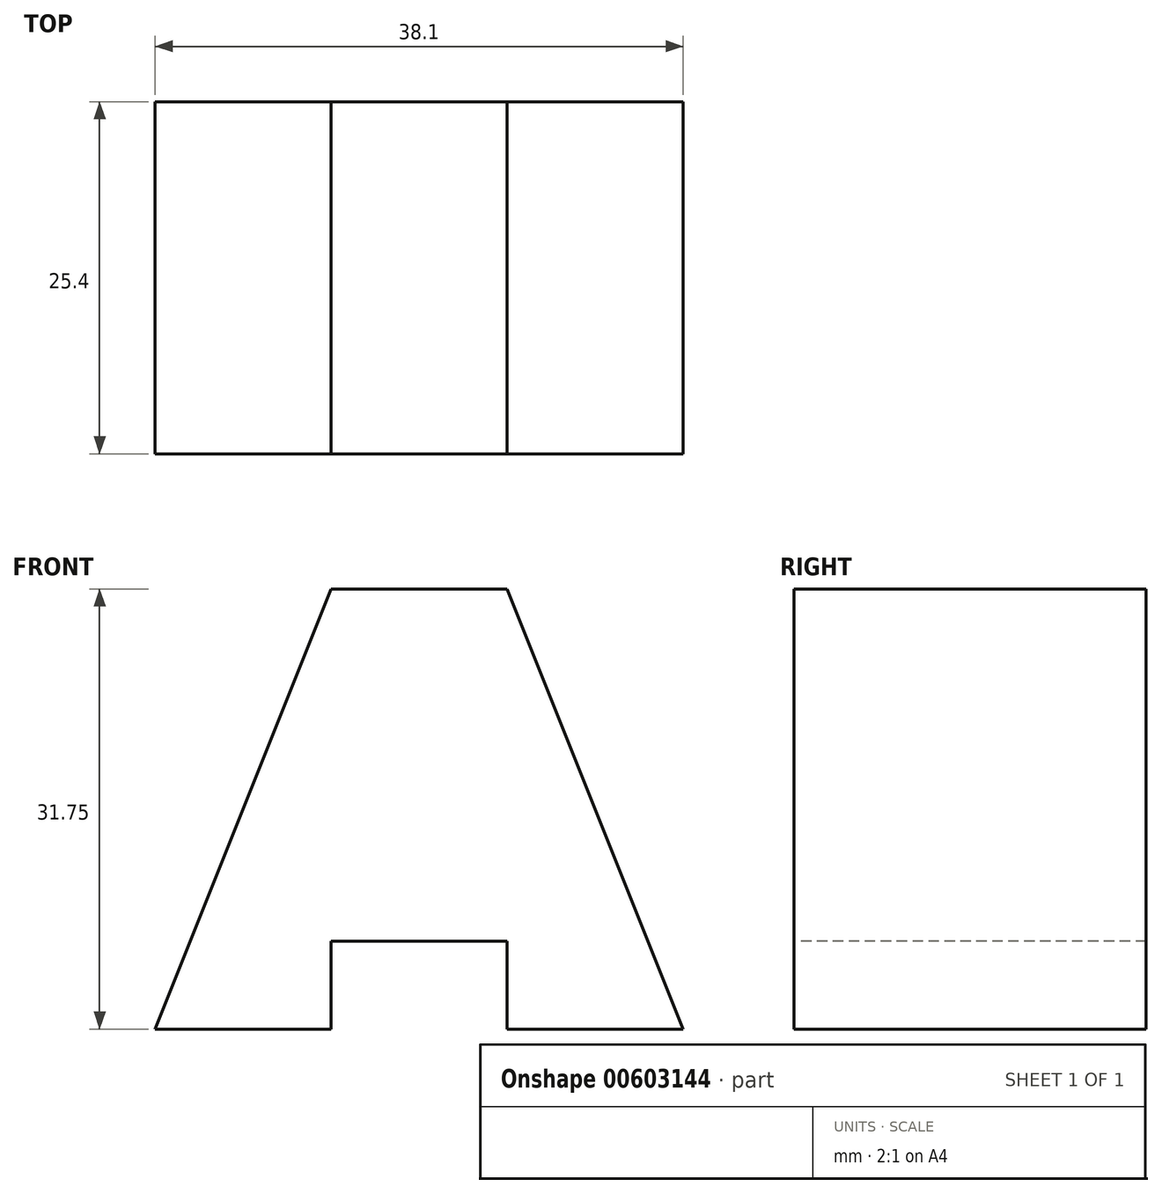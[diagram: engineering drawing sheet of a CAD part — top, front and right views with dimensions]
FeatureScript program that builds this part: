
annotation { "Feature Type Name" : "Feature", "Feature Type Description" : "" }
export const myFeature = defineFeature(function(context is Context, id is Id, definition is map)
    precondition{}
    {
        {
            var Q0;
            Q0=qCreatedBy(makeId("Front.planeOp"),FACE);
            var sketch = newSketch(context, id + "F0", { "sketchPlane" : qUnion([Q0])});
            skLineSegment(sketch, "E0", {"start": v(0, 0) * mm, "end": v(-19.05, 0) * mm});
            skLineSegment(sketch, "E1", {"start": v(-19.05, 0) * mm, "end": v(19.05, 0) * mm});
            skLineSegment(sketch, "E2", {"start": v(19.05, 0) * mm, "end": v(19.05, -31.75) * mm});
            skLineSegment(sketch, "E3", {"start": v(19.05, -31.75) * mm, "end": v(-19.05, -31.75) * mm});
            skLineSegment(sketch, "E4", {"start": v(-19.05, -31.75) * mm, "end": v(-19.05, 0) * mm});
            skSolve(sketch);
        }
        {
            var Q0;
            Q0 = qSketchRegion(id + "F0", true);
            extrude(context, id + "F1", {"entities" : qUnion([Q0]), "depth" : 25.4 * mm, "offsetDistance" : 25.4 * mm});
        }
        {
            var Q0;
            Q0=makeQuery(id+"F1.opExtrude","CAP_FACE",FACE,{"disambiguationData":[OSD([sQuery(id+"F0.wireOp",EDGE,"E1"),sQuery(id+"F0.wireOp",EDGE,"E2"),sQuery(id+"F0.wireOp",EDGE,"E3"),sQuery(id+"F0.wireOp",EDGE,"E4")])],"isStart":false});
            var sketch = newSketch(context, id + "F2", { "sketchPlane" : qUnion([Q0])});
            skLineSegment(sketch, "E5", {"start": v(-6.35, -31.75) * mm, "end": v(-6.35, -25.4) * mm});
            skLineSegment(sketch, "E6", {"start": v(-6.35, -25.4) * mm, "end": v(6.35, -25.4) * mm});
            skLineSegment(sketch, "E7", {"start": v(6.35, -25.4) * mm, "end": v(6.35, -31.75) * mm});
            skLineSegment(sketch, "E8", {"start": v(6.35, -31.75) * mm, "end": v(-6.35, -31.75) * mm});
            skSolve(sketch);
        }
        {
            var Q0;
            Q0 = qSketchRegion(id + "F2", true);
            extrude(context, id + "F3", {"entities" : qUnion([Q0]), "operationType" : NewBodyOperationType.REMOVE, "oppositeDirection" : true, "depth" : 25.4 * mm, "offsetDistance" : 25.4 * mm});
        }
        {
            var Q0;
            Q0=makeQuery(id+"F1.opExtrude","CAP_FACE",FACE,{"disambiguationData":[OSD([sQuery(id+"F0.wireOp",EDGE,"E1"),sQuery(id+"F0.wireOp",EDGE,"E2"),sQuery(id+"F0.wireOp",EDGE,"E3"),sQuery(id+"F0.wireOp",EDGE,"E4")])],"isStart":false});
            var sketch = newSketch(context, id + "F4", { "sketchPlane" : qUnion([Q0])});
            skLineSegment(sketch, "E9", {"start": v(-19.05, 0) * mm, "end": v(-6.35, 0) * mm});
            skLineSegment(sketch, "E10", {"start": v(-6.35, 0) * mm, "end": v(-19.05, -31.75) * mm});
            skLineSegment(sketch, "E11", {"start": v(-19.05, -31.75) * mm, "end": v(-19.05, 0) * mm});
            skSolve(sketch);
        }
        {
            var Q0;
            Q0 = qSketchRegion(id + "F4", true);
            extrude(context, id + "F5", {"entities" : qUnion([Q0]), "operationType" : NewBodyOperationType.REMOVE, "oppositeDirection" : true, "depth" : 25.4 * mm, "offsetDistance" : 25.4 * mm});
        }
        {
            var Q0;
            Q0=makeQuery(id+"F1.opExtrude","CAP_FACE",FACE,{"disambiguationData":[OSD([sQuery(id+"F0.wireOp",EDGE,"E1"),sQuery(id+"F0.wireOp",EDGE,"E2"),sQuery(id+"F0.wireOp",EDGE,"E3"),sQuery(id+"F0.wireOp",EDGE,"E4")])],"isStart":false});
            var sketch = newSketch(context, id + "F6", { "sketchPlane" : qUnion([Q0])});
            skLineSegment(sketch, "E12", {"start": v(19.05, 0) * mm, "end": v(6.35, 0) * mm});
            skLineSegment(sketch, "E13", {"start": v(6.35, 0) * mm, "end": v(19.05, -31.75) * mm});
            skLineSegment(sketch, "E14", {"start": v(19.05, -31.75) * mm, "end": v(19.05, 0) * mm});
            skSolve(sketch);
        }
        {
            var Q0;
            Q0 = qSketchRegion(id + "F6", true);
            extrude(context, id + "F7", {"entities" : qUnion([Q0]), "operationType" : NewBodyOperationType.REMOVE, "oppositeDirection" : true, "depth" : 25.4 * mm, "offsetDistance" : 25.4 * mm});
        }
    });
